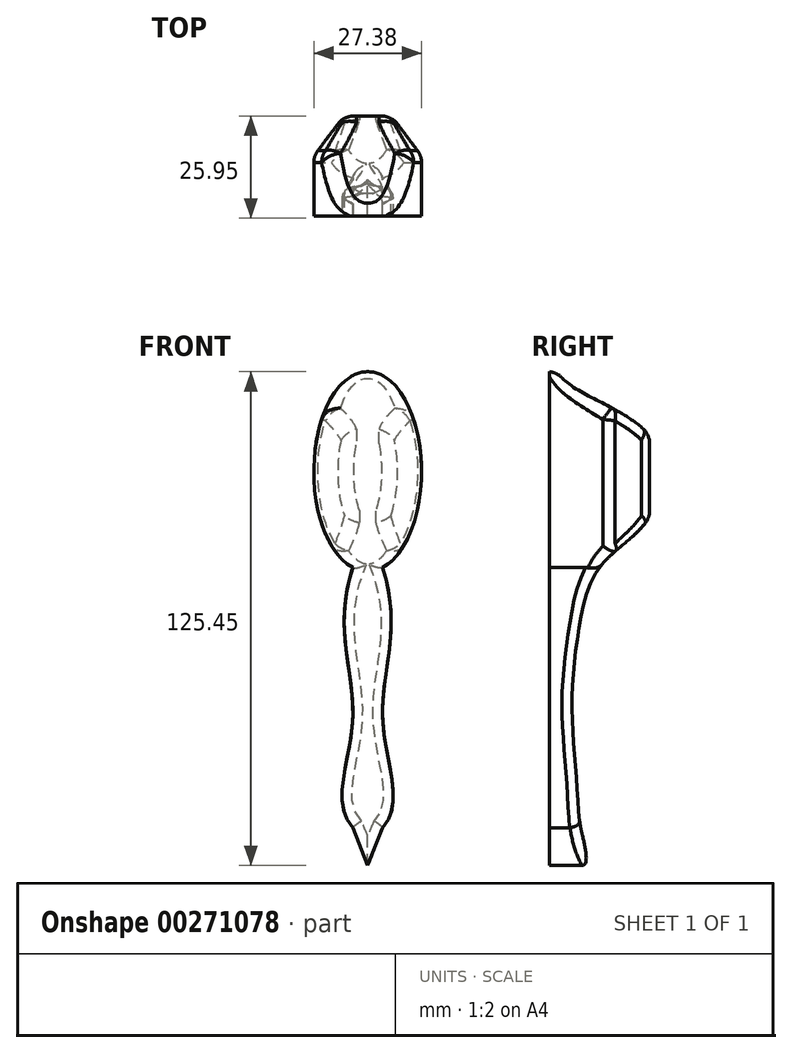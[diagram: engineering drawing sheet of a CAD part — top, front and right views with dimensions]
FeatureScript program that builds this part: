
annotation { "Feature Type Name" : "Feature", "Feature Type Description" : "" }
export const myFeature = defineFeature(function(context is Context, id is Id, definition is map)
    precondition{}
    {
        {
            var Q0;
            Q0=qCreatedBy(makeId("Front.planeOp"),FACE);
            var sketch = newSketch(context, id + "F0", { "sketchPlane" : qUnion([Q0])});
            skEllipse(sketch, "E0", {"center": v(-38.28, 64.98) * mm, "majorRadius": 25.4 * mm, "minorRadius": 13.69 * mm, "majorAxis": v(0, -1)});
            skLineSegment(sketch, "E1", {"start": v(-38.28, 90.38) * mm, "end": v(-38.28, -35.1) * mm, "construction": true});
            skPoint(sketch, "E1.endSnap0", {"position": v(-38.28, 39.58) * mm});
            skLineSegment(sketch, "E2", {"start": v(-38.28, -35.1) * mm, "end": v(-42.05, -25.5) * mm});
            skPoint(sketch, "E3.1.internal.orphan", {"position": v(-42.05, -16.24) * mm});
            skFitSpline(sketch, "E4", {"points": [v(-42.05, -25.5) * mm, v(-44.45, -13.16) * mm, v(-42.05, 3.3) * mm, v(-44.1, 23.19) * mm, v(-42.05, 40.57) * mm], "startDerivative": vector(-42.12, 46.65) * mm, "endDerivative": vector(21.67, 65.75) * mm});
            skFitSpline(sketch, "E5.MirrorCS", {"points": [v(-34.5, -25.5) * mm, v(-32.1, -13.16) * mm, v(-34.5, 3.3) * mm, v(-32.45, 23.19) * mm, v(-34.5, 40.57) * mm], "startDerivative": vector(42.12, 46.65) * mm, "endDerivative": vector(-21.67, 65.75) * mm});
            skLineSegment(sketch, "E6.MirrorCS", {"start": v(-38.28, -35.1) * mm, "end": v(-34.5, -25.5) * mm});
            skSolve(sketch);
        }
        {
            var Q0;
            {var subQ0=sQuery(id+"F0.wireOp",EDGE,"E0");var subQ1=makeQuery(id+"F0.imprint","INTERSECT",VERTEX,{"derivedFrom":[subQ0,sQuery(id+"F0.wireOp",EDGE,"E4")]});Q0=makeQuery(id+"F0.imprint","IMPRINT",FACE,{"disambiguationData":[TD([[makeQuery(id+"F0.imprint","IMPRINT",EDGE,{"disambiguationData":[TD([[subQ1,1.0]])],"derivedFrom":subQ0}),1.0]])]});}
            var Q1;
            Q1=makeQuery(id+"F0.imprint","IMPRINT",FACE,{"disambiguationData":[TD([[makeQuery(id+"F0.imprint","IMPRINT",EDGE,{"derivedFrom":sQuery(id+"F0.wireOp",EDGE,"E2")}),-1.0]])]});
            extrude(context, id + "F1", {"entities" : qUnion([Q0, Q1]), "depth" : 25.4 * mm});
        }
        {
            var Q0;
            Q0=qCreatedBy(makeId("Right.planeOp"),FACE);
            var sketch = newSketch(context, id + "F2", { "sketchPlane" : qUnion([Q0])});
            skFitSpline(sketch, "E7", {"points": [v(-12.14, -37.1) * mm, v(-18.4, -16.05) * mm, v(-19.75, 5.43) * mm, v(-17.96, 25.13) * mm, v(-12.5, 40.9) * mm, v(0, 53.45) * mm, v(0, 74.07) * mm, v(-22.88, 89.58) * mm, v(-18.32, 98.08) * mm, v(53.88, 66.1) * mm, v(32.56, -46.33) * mm, v(-12.14, -37.1) * mm]});
            skSolve(sketch);
        }
        {
            var Q0;
            Q0=makeQuery(id+"F2.imprint","IMPRINT",FACE,{"disambiguationData":[TD([[makeQuery(id+"F2.imprint","IMPRINT",EDGE,{"derivedFrom":sQuery(id+"F2.wireOp",EDGE,"E7")}),-1.0]])]});
            extrude(context, id + "F3", {"entities" : qUnion([Q0]), "operationType" : NewBodyOperationType.REMOVE, "endBound" : BoundingType.THROUGH_ALL, "oppositeDirection" : true, "depth" : 25.4 * mm});
        }
        {
            var Q0;
            Q0=makeQuery(id+"F3.boolean.opBoolean","INTERSECT",EDGE,{"derivedFrom":[makeQuery(id+"F1.opExtrude","SWEPT_FACE",FACE,{"disambiguationData":[OSD([sQuery(id+"F0.wireOp",EDGE,"E4")])]}),makeQuery(id+"F3.opExtrude","SWEPT_FACE",FACE,{"disambiguationData":[OSD([sQuery(id+"F2.wireOp",EDGE,"E7")])]})]});
            var Q1;
            Q1=makeQuery(id+"F3.boolean.opBoolean","INTERSECT",EDGE,{"derivedFrom":[makeQuery(id+"F1.opExtrude","SWEPT_FACE",FACE,{"disambiguationData":[OSD([sQuery(id+"F0.wireOp",EDGE,"E5.MirrorCS")])]}),makeQuery(id+"F3.opExtrude","SWEPT_FACE",FACE,{"disambiguationData":[OSD([sQuery(id+"F2.wireOp",EDGE,"E7")])]})]});
            var Q2;
            Q2=makeQuery(id+"F3.boolean.opBoolean","INTERSECT",EDGE,{"derivedFrom":[makeQuery(id+"F1.opExtrude","SWEPT_FACE",FACE,{"disambiguationData":[OSD([sQuery(id+"F0.wireOp",EDGE,"E2")])]}),makeQuery(id+"F3.opExtrude","SWEPT_FACE",FACE,{"disambiguationData":[OSD([sQuery(id+"F2.wireOp",EDGE,"E7")])]})]});
            var Q3;
            Q3=makeQuery(id+"F3.boolean.opBoolean","INTERSECT",EDGE,{"derivedFrom":[makeQuery(id+"F1.opExtrude","SWEPT_FACE",FACE,{"disambiguationData":[OSD([sQuery(id+"F0.wireOp",EDGE,"E6.MirrorCS")])]}),makeQuery(id+"F3.opExtrude","SWEPT_FACE",FACE,{"disambiguationData":[OSD([sQuery(id+"F2.wireOp",EDGE,"E7")])]})]});
            fillet(context, id + "F4", {"entities" : qUnion([Q0, Q1, Q2, Q3]), "radius" : 2.54 * mm, "tangentPropagation" : true, "allowEdgeOverflow" : false});
        }
        {
            var Q0;
            {var subQ0=sQuery(id+"F0.wireOp",EDGE,"E0");Q0=makeQuery(id+"F4.opFillet","BLEND_EDGE",EDGE,{"blendedFrom":[makeQuery(id+"F3.boolean.opBoolean","SPLIT",EDGE,{"disambiguationData":[OD(1.0)],"derivedFrom":makeQuery(id+"F1.opExtrude","CAP_EDGE",EDGE,{"disambiguationData":[OSD([subQ0])],"isStart":true})}),makeQuery(id+"F1.opExtrude","SWEPT_FACE",FACE,{"disambiguationData":[OSD([subQ0])]})],"blendedInto":[makeQuery(id+"F1.opExtrude","SWEPT_FACE",FACE,{"disambiguationData":[OSD([subQ0])]})]});}
            var Q1;
            {var subQ0=sQuery(id+"F0.wireOp",EDGE,"E0");Q1=makeQuery(id+"F4.opFillet","BLEND_EDGE",EDGE,{"blendedFrom":[makeQuery(id+"F3.boolean.opBoolean","SPLIT",EDGE,{"disambiguationData":[OD(0.0)],"derivedFrom":makeQuery(id+"F1.opExtrude","CAP_EDGE",EDGE,{"disambiguationData":[OSD([subQ0])],"isStart":true})}),makeQuery(id+"F1.opExtrude","SWEPT_FACE",FACE,{"disambiguationData":[OSD([subQ0])]})],"blendedInto":[makeQuery(id+"F1.opExtrude","SWEPT_FACE",FACE,{"disambiguationData":[OSD([subQ0])]})]});}
            var Q2;
            Q2=makeQuery(id+"F3.boolean.opBoolean","SPLIT",EDGE,{"disambiguationData":[OD(0.0)],"derivedFrom":makeQuery(id+"F1.opExtrude","CAP_EDGE",EDGE,{"disambiguationData":[OSD([sQuery(id+"F0.wireOp",EDGE,"E0")])],"isStart":true})});
            var Q3;
            Q3=makeQuery(id+"F3.boolean.opBoolean","SPLIT",EDGE,{"disambiguationData":[OD(1.0)],"derivedFrom":makeQuery(id+"F1.opExtrude","CAP_EDGE",EDGE,{"disambiguationData":[OSD([sQuery(id+"F0.wireOp",EDGE,"E0")])],"isStart":true})});
            chamfer(context, id + "F5", {"entities" : qUnion([Q0, Q1, Q2, Q3]), "chamferType" : ChamferType.TWO_OFFSETS, "width1" : 10.16 * mm, "oppositeDirection" : false, "width2" : 7.62 * mm, "tangentPropagation" : true});
        }
        {
            var Q0;
            {var subQ0=sQuery(id+"F0.wireOp",EDGE,"E0");Q0=makeQuery(id+"F5.opChamfer","BLEND_EDGE",EDGE,{"blendedFrom":[makeQuery(id+"F3.boolean.opBoolean","SPLIT",EDGE,{"disambiguationData":[OD(0.0)],"derivedFrom":makeQuery(id+"F1.opExtrude","CAP_EDGE",EDGE,{"disambiguationData":[OSD([subQ0])],"isStart":true})}),makeQuery(id+"F1.opExtrude","SWEPT_FACE",FACE,{"disambiguationData":[OSD([subQ0])]})],"blendedInto":[makeQuery(id+"F1.opExtrude","SWEPT_FACE",FACE,{"disambiguationData":[OSD([subQ0])]})]});}
            var Q1;
            {var subQ0=sQuery(id+"F0.wireOp",EDGE,"E0");Q1=makeQuery(id+"F5.opChamfer","BLEND_EDGE",EDGE,{"blendedFrom":[makeQuery(id+"F3.boolean.opBoolean","SPLIT",EDGE,{"disambiguationData":[OD(0.0)],"derivedFrom":makeQuery(id+"F1.opExtrude","CAP_EDGE",EDGE,{"disambiguationData":[OSD([subQ0])],"isStart":true})}),makeQuery(id+"F1.opExtrude","CAP_FACE",FACE,{"disambiguationData":[OSD([subQ0,sQuery(id+"F0.wireOp",EDGE,"E2"),sQuery(id+"F0.wireOp",EDGE,"E4"),sQuery(id+"F0.wireOp",EDGE,"E5.MirrorCS"),sQuery(id+"F0.wireOp",EDGE,"E6.MirrorCS")])],"isStart":true})],"blendedInto":[makeQuery(id+"F1.opExtrude","CAP_FACE",FACE,{"disambiguationData":[OSD([subQ0,sQuery(id+"F0.wireOp",EDGE,"E2"),sQuery(id+"F0.wireOp",EDGE,"E4"),sQuery(id+"F0.wireOp",EDGE,"E5.MirrorCS"),sQuery(id+"F0.wireOp",EDGE,"E6.MirrorCS")])],"isStart":true})]});}
            var Q2;
            Q2=makeQuery(id+"F3.boolean.opBoolean","INTERSECT",EDGE,{"disambiguationData":[OD(0.0)],"derivedFrom":[makeQuery(id+"F1.opExtrude","CAP_FACE",FACE,{"disambiguationData":[OSD([sQuery(id+"F0.wireOp",EDGE,"E0"),sQuery(id+"F0.wireOp",EDGE,"E2"),sQuery(id+"F0.wireOp",EDGE,"E4"),sQuery(id+"F0.wireOp",EDGE,"E5.MirrorCS"),sQuery(id+"F0.wireOp",EDGE,"E6.MirrorCS")])],"isStart":true}),makeQuery(id+"F3.opExtrude","SWEPT_FACE",FACE,{"disambiguationData":[OSD([sQuery(id+"F2.wireOp",EDGE,"E7")])]})]});
            var Q3;
            {var subQ0=sQuery(id+"F0.wireOp",EDGE,"E0");Q3=makeQuery(id+"F5.opChamfer","BLEND_EDGE",EDGE,{"blendedFrom":[makeQuery(id+"F3.boolean.opBoolean","SPLIT",EDGE,{"disambiguationData":[OD(0.0)],"derivedFrom":makeQuery(id+"F1.opExtrude","CAP_EDGE",EDGE,{"disambiguationData":[OSD([subQ0])],"isStart":true})}),makeQuery(id+"F3.boolean.opBoolean","COPY",FACE,{"disambiguationData":[TD([makeQuery(id+"F1.opExtrude","SWEPT_FACE",FACE,{"disambiguationData":[OSD([subQ0])]}),makeQuery(id+"F1.opExtrude","CAP_FACE",FACE,{"disambiguationData":[OSD([subQ0,sQuery(id+"F0.wireOp",EDGE,"E2"),sQuery(id+"F0.wireOp",EDGE,"E4"),sQuery(id+"F0.wireOp",EDGE,"E5.MirrorCS"),sQuery(id+"F0.wireOp",EDGE,"E6.MirrorCS")])],"isStart":true})])],"derivedFrom":makeQuery(id+"F3.opExtrude","SWEPT_FACE",FACE,{"disambiguationData":[OSD([sQuery(id+"F2.wireOp",EDGE,"E7")])]})})],"blendedInto":[makeQuery(id+"F3.boolean.opBoolean","COPY",FACE,{"disambiguationData":[TD([makeQuery(id+"F1.opExtrude","SWEPT_FACE",FACE,{"disambiguationData":[OSD([subQ0])]}),makeQuery(id+"F1.opExtrude","CAP_FACE",FACE,{"disambiguationData":[OSD([subQ0,sQuery(id+"F0.wireOp",EDGE,"E2"),sQuery(id+"F0.wireOp",EDGE,"E4"),sQuery(id+"F0.wireOp",EDGE,"E5.MirrorCS"),sQuery(id+"F0.wireOp",EDGE,"E6.MirrorCS")])],"isStart":true})])],"derivedFrom":makeQuery(id+"F3.opExtrude","SWEPT_FACE",FACE,{"disambiguationData":[OSD([sQuery(id+"F2.wireOp",EDGE,"E7")])]})})]});}
            var Q4;
            Q4=makeQuery(id+"F3.boolean.opBoolean","INTERSECT",EDGE,{"disambiguationData":[OD(2.0)],"derivedFrom":[makeQuery(id+"F1.opExtrude","SWEPT_FACE",FACE,{"disambiguationData":[OSD([sQuery(id+"F0.wireOp",EDGE,"E0")])]}),makeQuery(id+"F3.opExtrude","SWEPT_FACE",FACE,{"disambiguationData":[OSD([sQuery(id+"F2.wireOp",EDGE,"E7")])]})]});
            var Q5;
            {var subQ0=sQuery(id+"F0.wireOp",EDGE,"E0");Q5=makeQuery(id+"F5.opChamfer","BLEND_EDGE",EDGE,{"blendedFrom":[makeQuery(id+"F3.boolean.opBoolean","SPLIT",EDGE,{"disambiguationData":[OD(1.0)],"derivedFrom":makeQuery(id+"F1.opExtrude","CAP_EDGE",EDGE,{"disambiguationData":[OSD([subQ0])],"isStart":true})}),makeQuery(id+"F3.boolean.opBoolean","COPY",FACE,{"disambiguationData":[TD([makeQuery(id+"F1.opExtrude","SWEPT_FACE",FACE,{"disambiguationData":[OSD([subQ0])]}),makeQuery(id+"F1.opExtrude","CAP_FACE",FACE,{"disambiguationData":[OSD([subQ0,sQuery(id+"F0.wireOp",EDGE,"E2"),sQuery(id+"F0.wireOp",EDGE,"E4"),sQuery(id+"F0.wireOp",EDGE,"E5.MirrorCS"),sQuery(id+"F0.wireOp",EDGE,"E6.MirrorCS")])],"isStart":true})])],"derivedFrom":makeQuery(id+"F3.opExtrude","SWEPT_FACE",FACE,{"disambiguationData":[OSD([sQuery(id+"F2.wireOp",EDGE,"E7")])]})})],"blendedInto":[makeQuery(id+"F3.boolean.opBoolean","COPY",FACE,{"disambiguationData":[TD([makeQuery(id+"F1.opExtrude","SWEPT_FACE",FACE,{"disambiguationData":[OSD([subQ0])]}),makeQuery(id+"F1.opExtrude","CAP_FACE",FACE,{"disambiguationData":[OSD([subQ0,sQuery(id+"F0.wireOp",EDGE,"E2"),sQuery(id+"F0.wireOp",EDGE,"E4"),sQuery(id+"F0.wireOp",EDGE,"E5.MirrorCS"),sQuery(id+"F0.wireOp",EDGE,"E6.MirrorCS")])],"isStart":true})])],"derivedFrom":makeQuery(id+"F3.opExtrude","SWEPT_FACE",FACE,{"disambiguationData":[OSD([sQuery(id+"F2.wireOp",EDGE,"E7")])]})})]});}
            var Q6;
            Q6=makeQuery(id+"F3.boolean.opBoolean","INTERSECT",EDGE,{"disambiguationData":[OD(1.0)],"derivedFrom":[makeQuery(id+"F1.opExtrude","CAP_FACE",FACE,{"disambiguationData":[OSD([sQuery(id+"F0.wireOp",EDGE,"E0"),sQuery(id+"F0.wireOp",EDGE,"E2"),sQuery(id+"F0.wireOp",EDGE,"E4"),sQuery(id+"F0.wireOp",EDGE,"E5.MirrorCS"),sQuery(id+"F0.wireOp",EDGE,"E6.MirrorCS")])],"isStart":true}),makeQuery(id+"F3.opExtrude","SWEPT_FACE",FACE,{"disambiguationData":[OSD([sQuery(id+"F2.wireOp",EDGE,"E7")])]})]});
            var Q7;
            {var subQ0=sQuery(id+"F0.wireOp",EDGE,"E4");var subQ1=sQuery(id+"F0.wireOp",EDGE,"E2");var subQ2=sQuery(id+"F0.wireOp",EDGE,"E6.MirrorCS");var subQ3=sQuery(id+"F0.wireOp",EDGE,"E5.MirrorCS");var subQ4=sQuery(id+"F0.wireOp",EDGE,"E0");Q7=makeQuery(id+"F5.opChamfer","BLEND_EDGE",EDGE,{"blendedFrom":[makeQuery(id+"F3.boolean.opBoolean","SPLIT",EDGE,{"disambiguationData":[OD(0.0)],"derivedFrom":makeQuery(id+"F1.opExtrude","CAP_EDGE",EDGE,{"disambiguationData":[OSD([subQ4])],"isStart":true})}),makeQuery(id+"F3.boolean.opBoolean","COPY",FACE,{"disambiguationData":[TD([makeQuery(id+"F1.opExtrude","SWEPT_FACE",FACE,{"disambiguationData":[OSD([subQ4])]}),makeQuery(id+"F1.opExtrude","CAP_FACE",FACE,{"disambiguationData":[OSD([subQ4,subQ1,subQ0,subQ3,subQ2])],"isStart":true}),makeQuery(id+"F1.opExtrude","SWEPT_FACE",FACE,{"disambiguationData":[OSD([subQ1])]}),makeQuery(id+"F1.opExtrude","SWEPT_FACE",FACE,{"disambiguationData":[OSD([subQ0])]}),makeQuery(id+"F1.opExtrude","SWEPT_FACE",FACE,{"disambiguationData":[OSD([subQ3])]}),makeQuery(id+"F1.opExtrude","SWEPT_FACE",FACE,{"disambiguationData":[OSD([subQ2])]})])],"derivedFrom":makeQuery(id+"F3.opExtrude","SWEPT_FACE",FACE,{"disambiguationData":[OSD([sQuery(id+"F2.wireOp",EDGE,"E7")])]})})],"blendedInto":[makeQuery(id+"F3.boolean.opBoolean","COPY",FACE,{"disambiguationData":[TD([makeQuery(id+"F1.opExtrude","SWEPT_FACE",FACE,{"disambiguationData":[OSD([subQ4])]}),makeQuery(id+"F1.opExtrude","CAP_FACE",FACE,{"disambiguationData":[OSD([subQ4,subQ1,subQ0,subQ3,subQ2])],"isStart":true}),makeQuery(id+"F1.opExtrude","SWEPT_FACE",FACE,{"disambiguationData":[OSD([subQ1])]}),makeQuery(id+"F1.opExtrude","SWEPT_FACE",FACE,{"disambiguationData":[OSD([subQ0])]}),makeQuery(id+"F1.opExtrude","SWEPT_FACE",FACE,{"disambiguationData":[OSD([subQ3])]}),makeQuery(id+"F1.opExtrude","SWEPT_FACE",FACE,{"disambiguationData":[OSD([subQ2])]})])],"derivedFrom":makeQuery(id+"F3.opExtrude","SWEPT_FACE",FACE,{"disambiguationData":[OSD([sQuery(id+"F2.wireOp",EDGE,"E7")])]})})]});}
            var Q8;
            {var subQ0=sQuery(id+"F0.wireOp",EDGE,"E0");Q8=makeQuery(id+"F5.opChamfer","BLEND_EDGE",EDGE,{"blendedFrom":[makeQuery(id+"F3.boolean.opBoolean","SPLIT",EDGE,{"disambiguationData":[OD(1.0)],"derivedFrom":makeQuery(id+"F1.opExtrude","CAP_EDGE",EDGE,{"disambiguationData":[OSD([subQ0])],"isStart":true})}),makeQuery(id+"F1.opExtrude","CAP_FACE",FACE,{"disambiguationData":[OSD([subQ0,sQuery(id+"F0.wireOp",EDGE,"E2"),sQuery(id+"F0.wireOp",EDGE,"E4"),sQuery(id+"F0.wireOp",EDGE,"E5.MirrorCS"),sQuery(id+"F0.wireOp",EDGE,"E6.MirrorCS")])],"isStart":true})],"blendedInto":[makeQuery(id+"F1.opExtrude","CAP_FACE",FACE,{"disambiguationData":[OSD([subQ0,sQuery(id+"F0.wireOp",EDGE,"E2"),sQuery(id+"F0.wireOp",EDGE,"E4"),sQuery(id+"F0.wireOp",EDGE,"E5.MirrorCS"),sQuery(id+"F0.wireOp",EDGE,"E6.MirrorCS")])],"isStart":true})]});}
            var Q9;
            {var subQ0=sQuery(id+"F0.wireOp",EDGE,"E0");Q9=makeQuery(id+"F5.opChamfer","BLEND_EDGE",EDGE,{"blendedFrom":[makeQuery(id+"F3.boolean.opBoolean","SPLIT",EDGE,{"disambiguationData":[OD(1.0)],"derivedFrom":makeQuery(id+"F1.opExtrude","CAP_EDGE",EDGE,{"disambiguationData":[OSD([subQ0])],"isStart":true})}),makeQuery(id+"F1.opExtrude","SWEPT_FACE",FACE,{"disambiguationData":[OSD([subQ0])]})],"blendedInto":[makeQuery(id+"F1.opExtrude","SWEPT_FACE",FACE,{"disambiguationData":[OSD([subQ0])]})]});}
            var Q10;
            {var subQ0=sQuery(id+"F0.wireOp",EDGE,"E4");var subQ1=sQuery(id+"F0.wireOp",EDGE,"E2");var subQ2=sQuery(id+"F0.wireOp",EDGE,"E6.MirrorCS");var subQ3=sQuery(id+"F0.wireOp",EDGE,"E5.MirrorCS");var subQ4=sQuery(id+"F0.wireOp",EDGE,"E0");Q10=makeQuery(id+"F5.opChamfer","BLEND_EDGE",EDGE,{"blendedFrom":[makeQuery(id+"F3.boolean.opBoolean","SPLIT",EDGE,{"disambiguationData":[OD(1.0)],"derivedFrom":makeQuery(id+"F1.opExtrude","CAP_EDGE",EDGE,{"disambiguationData":[OSD([subQ4])],"isStart":true})}),makeQuery(id+"F3.boolean.opBoolean","COPY",FACE,{"disambiguationData":[TD([makeQuery(id+"F1.opExtrude","SWEPT_FACE",FACE,{"disambiguationData":[OSD([subQ4])]}),makeQuery(id+"F1.opExtrude","CAP_FACE",FACE,{"disambiguationData":[OSD([subQ4,subQ1,subQ0,subQ3,subQ2])],"isStart":true}),makeQuery(id+"F1.opExtrude","SWEPT_FACE",FACE,{"disambiguationData":[OSD([subQ1])]}),makeQuery(id+"F1.opExtrude","SWEPT_FACE",FACE,{"disambiguationData":[OSD([subQ0])]}),makeQuery(id+"F1.opExtrude","SWEPT_FACE",FACE,{"disambiguationData":[OSD([subQ3])]}),makeQuery(id+"F1.opExtrude","SWEPT_FACE",FACE,{"disambiguationData":[OSD([subQ2])]})])],"derivedFrom":makeQuery(id+"F3.opExtrude","SWEPT_FACE",FACE,{"disambiguationData":[OSD([sQuery(id+"F2.wireOp",EDGE,"E7")])]})})],"blendedInto":[makeQuery(id+"F3.boolean.opBoolean","COPY",FACE,{"disambiguationData":[TD([makeQuery(id+"F1.opExtrude","SWEPT_FACE",FACE,{"disambiguationData":[OSD([subQ4])]}),makeQuery(id+"F1.opExtrude","CAP_FACE",FACE,{"disambiguationData":[OSD([subQ4,subQ1,subQ0,subQ3,subQ2])],"isStart":true}),makeQuery(id+"F1.opExtrude","SWEPT_FACE",FACE,{"disambiguationData":[OSD([subQ1])]}),makeQuery(id+"F1.opExtrude","SWEPT_FACE",FACE,{"disambiguationData":[OSD([subQ0])]}),makeQuery(id+"F1.opExtrude","SWEPT_FACE",FACE,{"disambiguationData":[OSD([subQ3])]}),makeQuery(id+"F1.opExtrude","SWEPT_FACE",FACE,{"disambiguationData":[OSD([subQ2])]})])],"derivedFrom":makeQuery(id+"F3.opExtrude","SWEPT_FACE",FACE,{"disambiguationData":[OSD([sQuery(id+"F2.wireOp",EDGE,"E7")])]})})]});}
            var Q11;
            Q11=makeQuery(id+"F3.boolean.opBoolean","INTERSECT",EDGE,{"disambiguationData":[OD(1.0)],"derivedFrom":[makeQuery(id+"F1.opExtrude","SWEPT_FACE",FACE,{"disambiguationData":[OSD([sQuery(id+"F0.wireOp",EDGE,"E0")])]}),makeQuery(id+"F3.opExtrude","SWEPT_FACE",FACE,{"disambiguationData":[OSD([sQuery(id+"F2.wireOp",EDGE,"E7")])]})]});
            var Q12;
            Q12=makeQuery(id+"F3.boolean.opBoolean","INTERSECT",EDGE,{"disambiguationData":[OD(0.0)],"derivedFrom":[makeQuery(id+"F1.opExtrude","SWEPT_FACE",FACE,{"disambiguationData":[OSD([sQuery(id+"F0.wireOp",EDGE,"E0")])]}),makeQuery(id+"F3.opExtrude","SWEPT_FACE",FACE,{"disambiguationData":[OSD([sQuery(id+"F2.wireOp",EDGE,"E7")])]})]});
            var Q13;
            Q13=makeQuery(id+"F3.boolean.opBoolean","INTERSECT",EDGE,{"disambiguationData":[OD(0.0)],"derivedFrom":[makeQuery(id+"F1.opExtrude","SWEPT_FACE",FACE,{"disambiguationData":[OSD([sQuery(id+"F0.wireOp",EDGE,"E0")])]}),makeQuery(id+"F3.opExtrude","SWEPT_FACE",FACE,{"disambiguationData":[OSD([sQuery(id+"F2.wireOp",EDGE,"E7")])]})]});
            fillet(context, id + "F6", {"entities" : qUnion([Q0, Q1, Q2, Q3, Q4, Q5, Q6, Q7, Q8, Q9, Q10, Q11, Q12, Q13]), "radius" : 5.08 * mm, "tangentPropagation" : true, "allowEdgeOverflow" : false});
        }
    });
